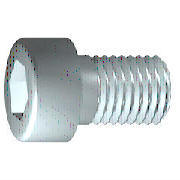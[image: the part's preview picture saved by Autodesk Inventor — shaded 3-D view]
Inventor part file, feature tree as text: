
AUTODESK INVENTOR PART (.ipt)
format: ipt  version: 2025 (Build 290162010, 162A)  size: 186,880 bytes
history: native  units: mm (DEFAULTED — no unit token found)
features: extrude x1, plane x1, fillet x1
ambient origin geometry x7: Origin, YZ Plane, XY Plane, X Axis, Y Axis, Z Axis, Center Point
bodies: Solid1 (feature_tree), Body (feature_tree)
feature tree (3):
  extrude  "Slot"  Depth=18.0mm
  plane  "Work Plane1"
  fillet  "Fillet2"  Radius=0.306825mm
